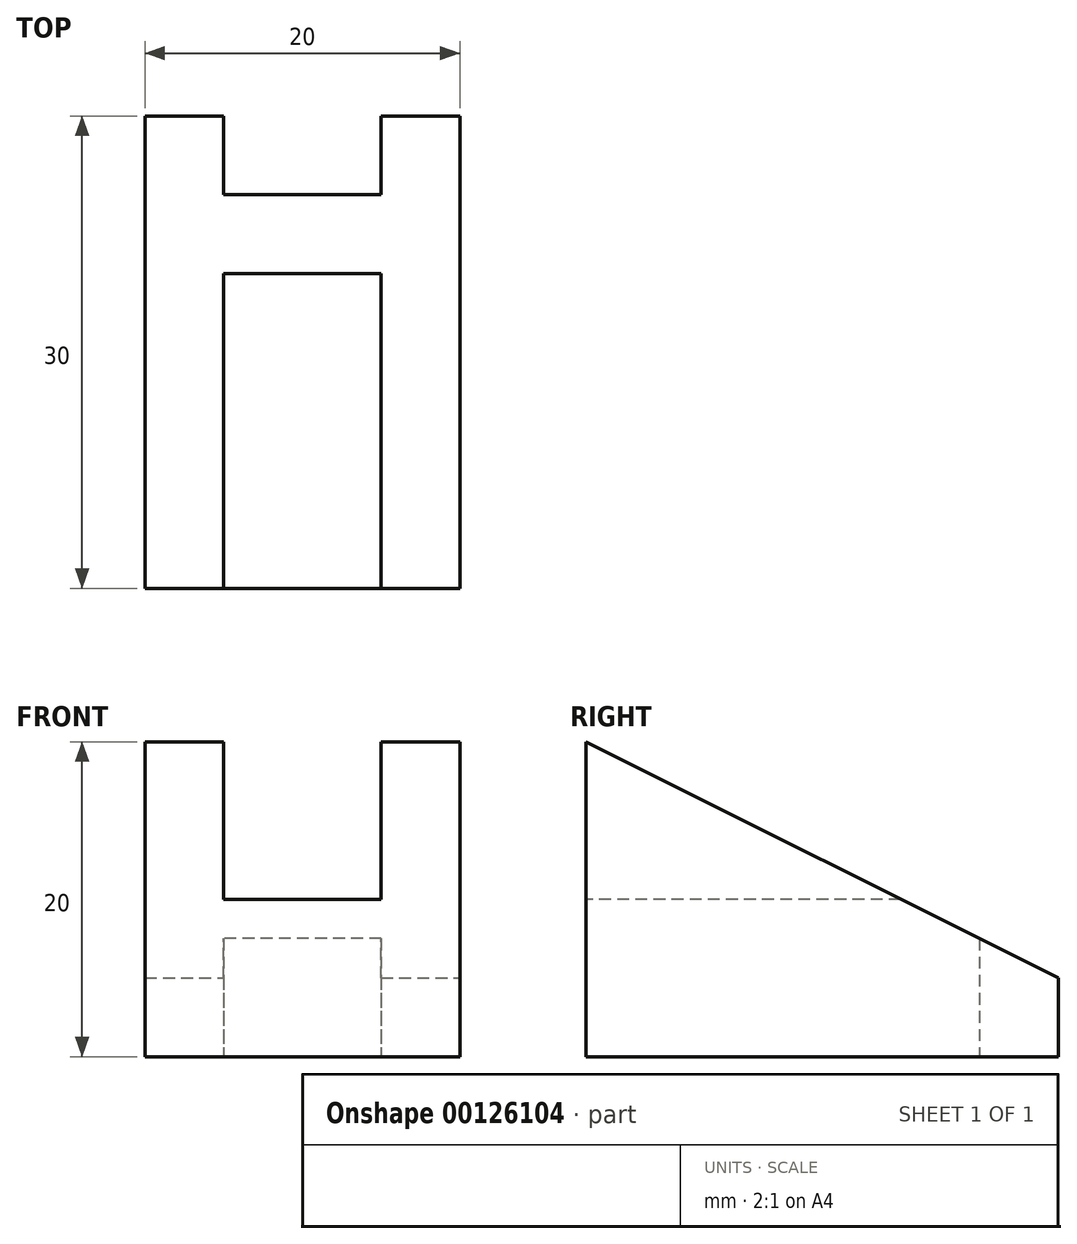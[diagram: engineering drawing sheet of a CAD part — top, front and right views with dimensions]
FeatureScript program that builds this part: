
annotation { "Feature Type Name" : "Feature", "Feature Type Description" : "" }
export const myFeature = defineFeature(function(context is Context, id is Id, definition is map)
    precondition{}
    {
        {
            var Q0;
            Q0=qCreatedBy(makeId("Front.planeOp"),FACE);
            var sketch = newSketch(context, id + "F0", { "sketchPlane" : qUnion([Q0])});
            skLineSegment(sketch, "E0", {"start": v(0, 0) * mm, "end": v(-10, 0) * mm});
            skLineSegment(sketch, "E1", {"start": v(-10, 0) * mm, "end": v(-10, 20) * mm});
            skLineSegment(sketch, "E2", {"start": v(-10, 20) * mm, "end": v(-5, 20) * mm});
            skLineSegment(sketch, "E3", {"start": v(-5, 20) * mm, "end": v(-5, 10) * mm});
            skLineSegment(sketch, "E4", {"start": v(-5, 10) * mm, "end": v(5, 10) * mm});
            skLineSegment(sketch, "E5", {"start": v(5, 10) * mm, "end": v(5, 20) * mm});
            skLineSegment(sketch, "E6", {"start": v(5, 20) * mm, "end": v(10, 20) * mm});
            skLineSegment(sketch, "E7", {"start": v(10, 20) * mm, "end": v(10, 0) * mm});
            skLineSegment(sketch, "E8", {"start": v(10, 0) * mm, "end": v(0, 0) * mm});
            skSolve(sketch);
        }
        {
            var Q0;
            Q0 = qSketchRegion(id + "F0", true);
            extrude(context, id + "F1", {"entities" : qUnion([Q0]), "oppositeDirection" : true, "depth" : 30 * mm});
        }
        {
            var Q0;
            Q0=qCreatedBy(makeId("Right.planeOp"),FACE);
            var sketch = newSketch(context, id + "F2", { "sketchPlane" : qUnion([Q0])});
            skLineSegment(sketch, "E9.0", {"start": v(30, 20) * mm, "end": v(0, 20) * mm});
            skLineSegment(sketch, "E9.1", {"start": v(30, 20) * mm, "end": v(30, 0) * mm});
            skLineSegment(sketch, "E10", {"start": v(0, 20) * mm, "end": v(30, 5) * mm});
            skSolve(sketch);
        }
        {
            var Q0;
            Q0 = qSketchRegion(id + "F2", true);
            extrude(context, id + "F3", {"entities" : qUnion([Q0]), "operationType" : NewBodyOperationType.REMOVE, "endBound" : BoundingType.THROUGH_ALL, "oppositeDirection" : true, "depth" : 25 * mm, "hasSecondDirection" : true, "secondDirectionBound" : SecondDirectionBoundingType.THROUGH_ALL, "secondDirectionOppositeDirection" : false, "secondDirectionDepth" : 25 * mm});
        }
        {
            var Q0;
            Q0=makeQuery(id+"F1.opExtrude","SWEPT_FACE",FACE,{"disambiguationData":[OSD([sQuery(id+"F0.wireOp",EDGE,"E0"),sQuery(id+"F0.wireOp",EDGE,"E8")])]});
            var sketch = newSketch(context, id + "F4", { "sketchPlane" : qUnion([Q0])});
            skLineSegment(sketch, "E11.0", {"start": v(10, -30) * mm, "end": v(-10, -30) * mm});
            skLineSegment(sketch, "E12.bottom", {"start": v(5, -30) * mm, "end": v(-5, -30) * mm});
            skLineSegment(sketch, "E12.top", {"start": v(5, -25) * mm, "end": v(-5, -25) * mm});
            skLineSegment(sketch, "E12.left", {"start": v(5, -30) * mm, "end": v(5, -25) * mm});
            skLineSegment(sketch, "E12.right", {"start": v(-5, -30) * mm, "end": v(-5, -25) * mm});
            skPoint(sketch, "E13", {"position": v(0, -30) * mm});
            skSolve(sketch);
        }
        {
            var Q0;
            Q0 = qSketchRegion(id + "F4", true);
            extrude(context, id + "F5", {"entities" : qUnion([Q0]), "operationType" : NewBodyOperationType.REMOVE, "endBound" : BoundingType.THROUGH_ALL, "oppositeDirection" : true, "depth" : 25 * mm});
        }
    });
